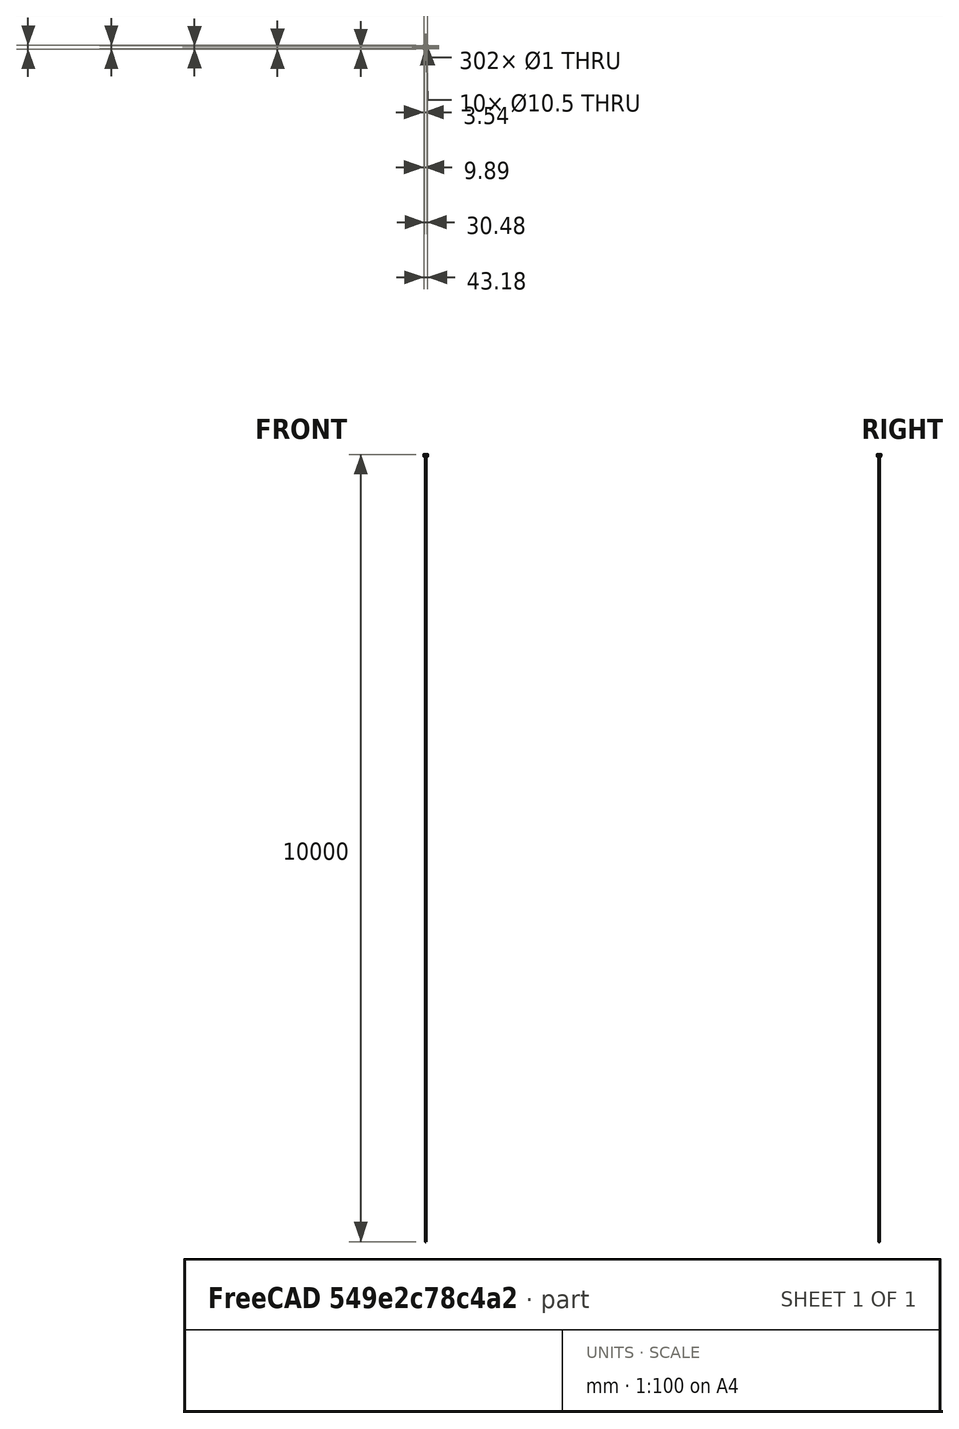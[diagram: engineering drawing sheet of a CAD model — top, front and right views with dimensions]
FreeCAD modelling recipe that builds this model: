
FCSTD DOCUMENT  (FreeCAD 0.14R3692 (Git))
Label: keypad-case
License: The MIT License
LicenseURL: http://opensource.org/licenses/MIT
objects: Part::Feature×39, Sketcher::SketchObject×5, Part::FeaturePython×5, PartDesign::Pocket×3, PartDesign::Pad×2, PartDesign::Mirrored×2, Part::Cylinder×2, Part::MultiFuse×2, Part::Compound×1, Part::Thickness×1, PartDesign::MultiTransform×1, Part::Cone×1, Part::Cut×1, PartDesign::PolarPattern×1, App::DocumentObjectGroup×1, Part::Chamfer×1
note: 72 computed .brp shape members not serialized (recipe doc carries the construction recipe); baked Part::Feature solids carry a one-line shape summary decoded from their .brp

FEATURE [Part::Feature] Part__Feature  label="R1"
  shape: bbox 2.25 x 18.49 x 4.625 mm, 14 faces (baked)
FEATURE [Part::Feature] Part__Feature001  label="R2"
  shape: bbox 2.25 x 15.95 x 4.625 mm, 14 faces (baked)
FEATURE [Part::Feature] Part__Feature002  label="R3"
  shape: bbox 2.25 x 15.95 x 4.625 mm, 14 faces (baked)
FEATURE [Part::Feature] Part__Feature003  label="R4"
  shape: bbox 2.25 x 10.87 x 4.625 mm, 14 faces (baked)
FEATURE [Part::Feature] Part__Feature004  label="R5"
  shape: bbox 2.25 x 10.87 x 4.625 mm, 14 faces (baked)
FEATURE [Part::Feature] Part__Feature005  label="R6"
  shape: bbox 2.25 x 13.41 x 4.625 mm, 14 faces (baked)
FEATURE [Part::Feature] Part__Feature006  label="R7"
  shape: bbox 2.25 x 10.87 x 4.625 mm, 14 faces (baked)
FEATURE [Part::Feature] Part__Feature007  label="connector"
  shape: bbox 13.65 x 7.62 x 9.1 mm, 63 faces (baked)
FEATURE [Part::Feature] Part__Feature008  label="pushbutton-mini-001"
  shape: bbox 6.2 x 6.2 x 5.2 mm, 41 faces (baked)
FEATURE [Part::Feature] Part__Feature009  label="pushbutton-mini-002"
  shape: bbox 0.922 x 0.7 x 4.6 mm, 20 faces (baked)
FEATURE [Part::Feature] Part__Feature010  label="pushbutton-mini-003"
  shape: bbox 0.922 x 0.7 x 4.6 mm, 20 faces (baked)
FEATURE [Part::Feature] Part__Feature011  label="pushbutton-mini-004"
  shape: bbox 0.922 x 0.7 x 4.6 mm, 20 faces (baked)
FEATURE [Part::Feature] Part__Feature012  label="pushbutton-mini-005"
  shape: bbox 0.922 x 0.7 x 4.6 mm, 20 faces (baked)
FEATURE [Part::Feature] Part__Feature013  label="pushbutton-mini-006"
  shape: bbox 6.2 x 6.2 x 0.2 mm, 15 faces (baked)
FEATURE [Part::Feature] Part__Feature014  label="pushbutton-mini-007"
  shape: bbox 6.2 x 6.2 x 5.2 mm, 41 faces (baked)
FEATURE [Part::Feature] Part__Feature015  label="pushbutton-mini-008"
  shape: bbox 0.922 x 0.7 x 4.6 mm, 20 faces (baked)
FEATURE [Part::Feature] Part__Feature016  label="pushbutton-mini-009"
  shape: bbox 0.922 x 0.7 x 4.6 mm, 20 faces (baked)
FEATURE [Part::Feature] Part__Feature017  label="pushbutton-mini-010"
  shape: bbox 0.922 x 0.7 x 4.6 mm, 20 faces (baked)
FEATURE [Part::Feature] Part__Feature018  label="pushbutton-mini-011"
  shape: bbox 0.922 x 0.7 x 4.6 mm, 20 faces (baked)
FEATURE [Part::Feature] Part__Feature019  label="pushbutton-mini-012"
  shape: bbox 6.2 x 6.2 x 0.2 mm, 15 faces (baked)
FEATURE [Part::Feature] Part__Feature020  label="pushbutton-mini-013"
  shape: bbox 6.2 x 6.2 x 5.2 mm, 41 faces (baked)
FEATURE [Part::Feature] Part__Feature021  label="pushbutton-mini-014"
  shape: bbox 0.922 x 0.7 x 4.6 mm, 20 faces (baked)
FEATURE [Part::Feature] Part__Feature022  label="pushbutton-mini-015"
  shape: bbox 0.922 x 0.7 x 4.6 mm, 20 faces (baked)
FEATURE [Part::Feature] Part__Feature023  label="pushbutton-mini-016"
  shape: bbox 0.922 x 0.7 x 4.6 mm, 20 faces (baked)
FEATURE [Part::Feature] Part__Feature024  label="pushbutton-mini-017"
  shape: bbox 0.922 x 0.7 x 4.6 mm, 20 faces (baked)
FEATURE [Part::Feature] Part__Feature025  label="pushbutton-mini-018"
  shape: bbox 6.2 x 6.2 x 0.2 mm, 15 faces (baked)
FEATURE [Part::Feature] Part__Feature026  label="pushbutton-mini-019"
  shape: bbox 6.2 x 6.2 x 5.2 mm, 41 faces (baked)
FEATURE [Part::Feature] Part__Feature027  label="pushbutton-mini-020"
  shape: bbox 0.922 x 0.7 x 4.6 mm, 20 faces (baked)
FEATURE [Part::Feature] Part__Feature028  label="pushbutton-mini-021"
  shape: bbox 0.922 x 0.7 x 4.6 mm, 20 faces (baked)
FEATURE [Part::Feature] Part__Feature029  label="pushbutton-mini-022"
  shape: bbox 0.922 x 0.7 x 4.6 mm, 20 faces (baked)
FEATURE [Part::Feature] Part__Feature030  label="pushbutton-mini-023"
  shape: bbox 0.922 x 0.7 x 4.6 mm, 20 faces (baked)
FEATURE [Part::Feature] Part__Feature031  label="pushbutton-mini-024"
  shape: bbox 6.2 x 6.2 x 0.2 mm, 15 faces (baked)
FEATURE [Part::Feature] Part__Feature032  label="pushbutton-mini-025"
  shape: bbox 6.2 x 6.2 x 5.2 mm, 41 faces (baked)
FEATURE [Part::Feature] Part__Feature033  label="pushbutton-mini-026"
  shape: bbox 0.922 x 0.7 x 4.6 mm, 20 faces (baked)
FEATURE [Part::Feature] Part__Feature034  label="pushbutton-mini-027"
  shape: bbox 0.922 x 0.7 x 4.6 mm, 20 faces (baked)
FEATURE [Part::Feature] Part__Feature035  label="pushbutton-mini-028"
  shape: bbox 0.922 x 0.7 x 4.6 mm, 20 faces (baked)
FEATURE [Part::Feature] Part__Feature036  label="pushbutton-mini-029"
  shape: bbox 0.922 x 0.7 x 4.6 mm, 20 faces (baked)
FEATURE [Part::Feature] Part__Feature037  label="pushbutton-mini-030"
  shape: bbox 6.2 x 6.2 x 0.2 mm, 15 faces (baked)
FEATURE [Part::Feature] Part__Feature038  label="perfboard"
  shape: bbox 48.26 x 45.72 x 1.5 mm, 312 faces (baked)
FEATURE [Part::Compound] Compound  label="keypad"
  Links = -> [Part__Feature,Part__Feature008,Part__Feature009,Part__Feature010,Part__Feature007,Part__Feature006,Part__Feature005,Part__Feature004,Part__Feature018,Part__Feature020,Part__Feature017,Part__Feature021,Part__Feature022,Part__Feature023,Part__Feature024,Part__Feature026,Part__Feature025,Part__Feature033,Part__Feature027,Part__Feature028,Part__Feature029,Part__Feature002,Part__Feature003,+16 more]
  Placement = pos=(-19.05,-17.78,1.5) rot=(0,0,1;0rad)
FEATURE [Sketcher::SketchObject] Sketch  label="case-sketch"
  sketch-geometry (4):
    g0: LineSegment StartX=-24.13 StartY=-22.86 StartZ=0 EndX=24.13 EndY=-22.86 EndZ=0
    g1: LineSegment StartX=24.13 StartY=-22.86 StartZ=0 EndX=24.13 EndY=22.86 EndZ=0
    g2: LineSegment StartX=24.13 StartY=22.86 StartZ=0 EndX=-24.13 EndY=22.86 EndZ=0
    g3: LineSegment StartX=-24.13 StartY=22.86 StartZ=0 EndX=-24.13 EndY=-22.86 EndZ=0
  constraints (11):
    c: Coincident(g0,g1)
    c: Coincident(g1,g2)
    c: Coincident(g2,g3)
    c: Coincident(g3,g0)
    c: Horizontal(g0)
    c: Horizontal(g2)
    c: Vertical(g1)
    c: Vertical(g3)
    c: DistanceY(g1) = 45.72
    c: DistanceX(g0) = 48.26
    c: Symmetric(g0,g1,g-1)
FEATURE [PartDesign::Pad] Pad  label="case-pad"
  Length = 9.5
  Length2 = 100
  Sketch = -> Sketch
  Type = 0
FEATURE [Part::Thickness] Thickness  label="case-thickness"
  Faces = -> Pad [Face5]
  Intersection = false
  Join = 0
  Mode = 0
  SelfIntersection = false
  Value = 1
FEATURE [Sketcher::SketchObject] Sketch001  label="corner-sketch"
  Placement = pos=(0,0,9.5) rot=(1,0,0;3.14159rad)
  Support = -> Thickness [Face5]
  sketch-geometry (9):
    g0: LineSegment [constr] StartX=-19.05 StartY=17.78 StartZ=0 EndX=19.05 EndY=17.78 EndZ=0
    g1: LineSegment [constr] StartX=19.05 StartY=17.78 StartZ=0 EndX=19.05 EndY=-17.78 EndZ=0
    g2: LineSegment [constr] StartX=19.05 StartY=-17.78 StartZ=0 EndX=-19.05 EndY=-17.78 EndZ=0
    g3: LineSegment [constr] StartX=-19.05 StartY=-17.78 StartZ=0 EndX=-19.05 EndY=17.78 EndZ=0
    g4: ArcOfCircle CenterX=-19.05 CenterY=-17.78 CenterZ=0 NormalX=0 NormalY=0 NormalZ=1 Radius=4 StartAngle=0 EndAngle=1.5708
    g5: LineSegment StartX=-19.05 StartY=-13.78 StartZ=0 EndX=-24.63 EndY=-13.78 EndZ=0
    g6: LineSegment StartX=-24.63 StartY=-13.78 StartZ=0 EndX=-24.63 EndY=-23.36 EndZ=0
    g7: LineSegment StartX=-24.63 StartY=-23.36 StartZ=0 EndX=-15.05 EndY=-23.36 EndZ=0
    g8: LineSegment StartX=-15.05 StartY=-23.36 StartZ=0 EndX=-15.05 EndY=-17.78 EndZ=0
  constraints (24):
    c: Coincident(g2,g3)
    c: Horizontal(g0)
    c: Horizontal(g2)
    c: Vertical(g1)
    c: Vertical(g3)
    c: DistanceX(g2) = -38.1
    c: DistanceY(g1) = -35.56
    c: Coincident(g4,g2)
    c: Horizontal(g5)
    c: Coincident(g5,g6)
    c: Vertical(g6)
    c: Coincident(g6,g7)
    c: Horizontal(g7)
    c: Coincident(g7,g8)
    c: Vertical(g8)
    c: Tangent(g4,g8)
    c: Tangent(g4,g5)
    c: Symmetric(g2,g0,g-1)
    c: Radius(g4) = 4
    c: DistanceX(g5) = -5.58
    c: Equal(g5,g8)
    c: Coincident(g0,g3)
    c: Coincident(g0,g1)
    c: Coincident(g1,g2)
FEATURE [PartDesign::Pad] Pad001  label="corner-pad"
  Length = 6.5
  Length2 = 100
  Sketch = -> Sketch001
  Type = 0
FEATURE [PartDesign::Mirrored] Mirrored  label="corners-mirrored-horizontal"
  MirrorPlane = -> Sketch001 [V_Axis]
FEATURE [PartDesign::Mirrored] Mirrored001  label="corners-mirrored-vertical"
  MirrorPlane = -> Sketch001 [H_Axis]
FEATURE [PartDesign::MultiTransform] MultiTransform  label="corners-multi-transform"
  Originals = -> [Pad001]
  Transformations = -> [Mirrored,Mirrored001]
FEATURE [Part::Cylinder] Cylinder  label="screw-cylinder"
  Angle = 360
  Height = 10
  Radius = 1.75
FEATURE [Part::Cone] Cone  label="screw-cone"
  Angle = 360
  Height = 2
  Placement = pos=(0,0,9) rot=(0,0,1;0rad)
  Radius1 = 1
  Radius2 = 3
FEATURE [Part::Cylinder] Cylinder001  label="screw-head-cylinder"
  Angle = 360
  Height = 4
  Placement = pos=(0,0,11) rot=(0,0,1;0rad)
  Radius = 3
FEATURE [Part::MultiFuse] Fusion  label="screw-fusion"
  Shapes = -> [Cylinder001,Cone,Cylinder]
FEATURE [Part::FeaturePython] Clone  label="screw-fusion-front-left"  # Draft clone (typed FeaturePython)
  Objects = -> [Fusion]
  Placement = pos=(-19.05,17.78,-3.25) rot=(0,0,1;0rad)
  Scale = (1,1,1)
FEATURE [Part::FeaturePython] Clone001  label="screw-fusion-front-right"  # Draft clone (typed FeaturePython)
  Objects = -> [Fusion]
  Placement = pos=(19.05,17.78,-3.25) rot=(0,0,1;0rad)
  Scale = (1,1,1)
FEATURE [Part::FeaturePython] Clone002  label="screw-fusion-rear-right"  # Draft clone (typed FeaturePython)
  Objects = -> [Fusion]
  Placement = pos=(19.05,-17.78,-3.25) rot=(0,0,1;0rad)
  Scale = (1,1,1)
FEATURE [Part::MultiFuse] Fusion001  label="screws-fusion"
  Shapes = -> [Clone,Clone002,Clone001]
FEATURE [Part::Cut] Cut  label="screws-cut"
  Base = -> MultiTransform
  Tool = -> Fusion001
FEATURE [Sketcher::SketchObject] Sketch002  label="button-center-hole-sketch"
  Placement = pos=(0,0,10.5) rot=(0,0,1;0rad)
  Support = -> Cut [Face45]
  sketch-geometry (1):
    g0: Circle CenterX=0 CenterY=0 CenterZ=0 NormalX=0 NormalY=0 NormalZ=1 Radius=5.25
  constraints (2):
    c: Radius(g0) = 5.25
    c: Coincident(g0,g-1)
FEATURE [PartDesign::Pocket] Pocket  label="button-center-hole-pocket"
  Length = 5
  Sketch = -> Sketch002
  Type = 1
FEATURE [Sketcher::SketchObject] Sketch003  label="button-right-hole-sketch"
  Placement = pos=(0,0,10.5) rot=(0,0,1;0rad)
  Support = -> Pocket [Face34]
  sketch-geometry (1):
    g0: Circle CenterX=15.24 CenterY=0 CenterZ=0 NormalX=0 NormalY=0 NormalZ=1 Radius=5.25
  constraints (3):
    c: Radius(g0) = 5.25
    c: PointOnObject(g0,g-1)
    c: DistanceX(g-1,g0) = 15.24
FEATURE [PartDesign::Pocket] Pocket001  label="button-right-hole-pocket"
  Length = 5
  Sketch = -> Sketch003
  Type = 1
FEATURE [PartDesign::PolarPattern] PolarPattern  label="button-holes-polar-pattern"
  Angle = 360
  Axis = -> Sketch003 [N_Axis]
  Occurrences = 4
  Originals = -> [Pocket001]
FEATURE [Sketcher::SketchObject] Sketch004  label="connector-hole-sketch"
  Placement = pos=(-25.13,0,0) rot=(0.57735,-0.57735,-0.57735;2.0944rad)
  Support = -> PolarPattern [Face34]
  sketch-geometry (5):
    g0: LineSegment StartX=13.28 StartY=9.5 StartZ=0 EndX=22.28 EndY=9.5 EndZ=0
    g1: LineSegment StartX=22.28 StartY=9.5 StartZ=0 EndX=22.28 EndY=2.5 EndZ=0
    g2: LineSegment StartX=22.28 StartY=2.5 StartZ=0 EndX=13.28 EndY=2.5 EndZ=0
    g3: LineSegment StartX=13.28 StartY=2.5 StartZ=0 EndX=13.28 EndY=9.5 EndZ=0
    g4: GeomPoint [constr] X=17.78 Y=9.5 Z=0
  constraints (14):
    c: Coincident(g0,g1)
    c: Coincident(g1,g2)
    c: Coincident(g2,g3)
    c: Coincident(g3,g0)
    c: Horizontal(g0)
    c: Horizontal(g2)
    c: Vertical(g1)
    c: Vertical(g3)
    c: DistanceX(g2) = -9
    c: DistanceY(g1) = -7
    c: PointOnObject(g4,g0)
    c: Symmetric(g0,g0,g4)
    c: DistanceX(g-1,g4) = 17.78
    c: DistanceY(g-1,g2) = 2.5
FEATURE [PartDesign::Pocket] Pocket002  label="connector-hole-pocket"
  Length = 11
  Sketch = -> Sketch004
  Type = 0
FEATURE [Part::FeaturePython] Clone003  label="keypad-case"  # Draft clone (typed FeaturePython)
  Objects = -> [Pocket002]
  Scale = (1,1,1)
FEATURE [App::DocumentObjectGroup] Group  label="components"
  Group = -> [Compound]
FEATURE [Part::Chamfer] Chamfer  label="printing-chamfer"
  Base = -> Clone003
  Edges = 8 edges r=0.5: [Edge110,Edge113,Edge115,Edge117,Edge122,Edge123,Edge124,Edge125]
FEATURE [Part::FeaturePython] Clone004  label="keypad-case (printing)"  # Draft clone (typed FeaturePython)
  Objects = -> [Chamfer]
  Placement = pos=(0,0,0) rot=(0,1,0;3.14159rad)
  Scale = (1,1,1)
